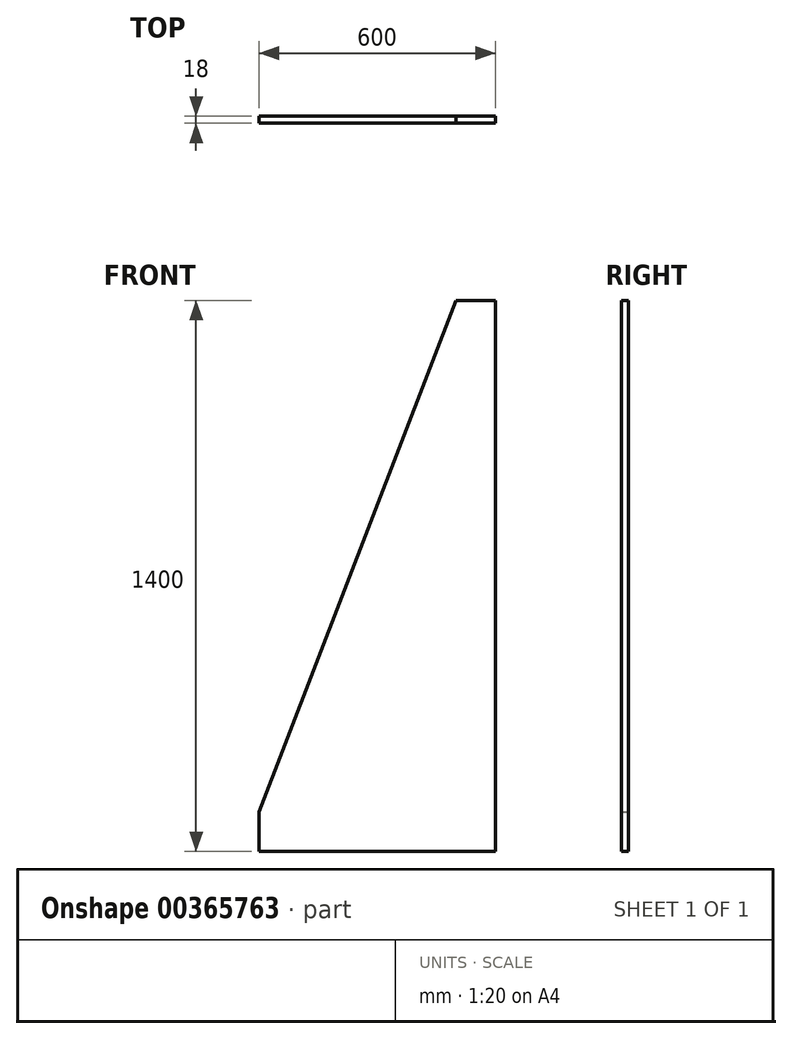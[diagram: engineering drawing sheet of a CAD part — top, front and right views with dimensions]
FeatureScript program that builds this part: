
annotation { "Feature Type Name" : "Feature", "Feature Type Description" : "" }
export const myFeature = defineFeature(function(context is Context, id is Id, definition is map)
    precondition{}
    {
        {
            var Q0;
            Q0=qCreatedBy(makeId("Front.planeOp"),FACE);
            var sketch = newSketch(context, id + "F0", { "sketchPlane" : qUnion([Q0])});
            skLineSegment(sketch, "E0", {"start": v(0, 0) * mm, "end": v(-600, 0) * mm});
            skLineSegment(sketch, "E1", {"start": v(-600, 0) * mm, "end": v(-600, 100) * mm});
            skLineSegment(sketch, "E2", {"start": v(-600, 100) * mm, "end": v(-100, 1400) * mm});
            skLineSegment(sketch, "E3", {"start": v(-100, 1400) * mm, "end": v(0, 1400) * mm});
            skLineSegment(sketch, "E4", {"start": v(0, 1400) * mm, "end": v(0, 0) * mm});
            skSolve(sketch);
        }
        {
            var Q0;
            Q0=makeQuery(id+"F0.imprint","IMPRINT",FACE,{"disambiguationData":[TD([[makeQuery(id+"F0.imprint","IMPRINT",EDGE,{"derivedFrom":sQuery(id+"F0.wireOp",EDGE,"E0")}),-1.0]])]});
            extrude(context, id + "F1", {"entities" : qUnion([Q0]), "depth" : 18 * mm});
        }
    });
